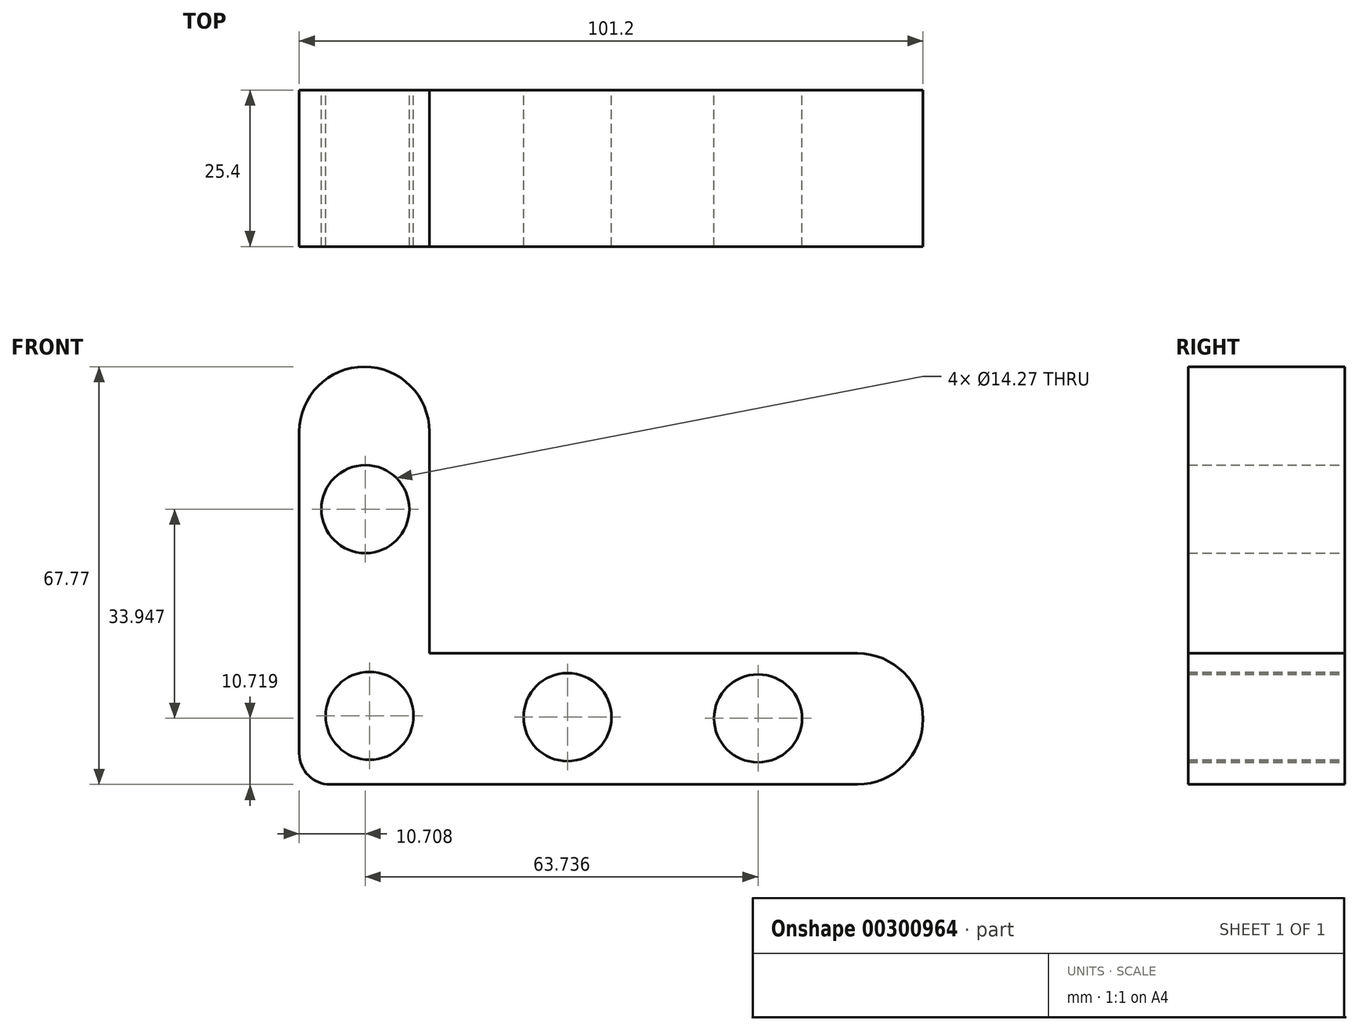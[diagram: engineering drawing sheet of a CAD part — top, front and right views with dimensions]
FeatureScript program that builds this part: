
annotation { "Feature Type Name" : "Feature", "Feature Type Description" : "" }
export const myFeature = defineFeature(function(context is Context, id is Id, definition is map)
    precondition{}
    {
        {
            var Q0;
            Q0=qCreatedBy(makeId("Front.planeOp"),FACE);
            var sketch = newSketch(context, id + "F0", { "sketchPlane" : qUnion([Q0])});
            skLineSegment(sketch, "E0.bottom", {"start": v(-57.98, 0) * mm, "end": v(32.59, 0) * mm});
            skLineSegment(sketch, "E0.top", {"start": v(-52.98, -21.26) * mm, "end": v(32.59, -21.26) * mm});
            skLineSegment(sketch, "E0.left", {"start": v(-57.98, 0) * mm, "end": v(-57.98, -16.26) * mm});
            skLineSegment(sketch, "E1.bottom", {"start": v(-57.98, 0) * mm, "end": v(-36.87, 0) * mm});
            skLineSegment(sketch, "E1.left", {"start": v(-57.98, 0) * mm, "end": v(-57.98, 35.95) * mm});
            skLineSegment(sketch, "E1.right", {"start": v(-36.87, 0) * mm, "end": v(-36.87, 35.95) * mm});
            skCircle(sketch, "E2", {"center": v(-47.27, 23.4) * mm, "radius": 7.14 * mm});
            skCircle(sketch, "E3", {"center": v(-46.58, -10.14) * mm, "radius": 7.14 * mm});
            skCircle(sketch, "E4", {"center": v(-14.46, -10.34) * mm, "radius": 7.14 * mm});
            skCircle(sketch, "E5", {"center": v(16.46, -10.54) * mm, "radius": 7.14 * mm});
            skArc(sketch, "E6", {"start": v(-36.87, 35.95) * mm, "mid": v(-47.42, 46.5) * mm, "end": v(-57.98, 35.95) * mm});
            skArc(sketch, "E7", {"start": v(32.59, -21.26) * mm, "mid": v(43.22, -10.63) * mm, "end": v(32.59, 0) * mm});
            skPoint(sketch, "E8.visualSharp", {"position": v(-57.98, -21.26) * mm});
            skArc(sketch, "E8.filletArc", {"start": v(-57.98, -16.26) * mm, "mid": v(-56.52, -19.8) * mm, "end": v(-52.98, -21.26) * mm});
            skSolve(sketch);
        }
        {
            var Q0;
            Q0 = qSketchRegion(id + "F0", true);
            extrude(context, id + "F1", {"entities" : qUnion([Q0]), "depth" : 25.4 * mm});
        }
    });
